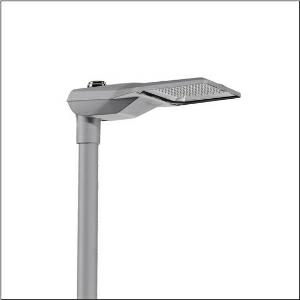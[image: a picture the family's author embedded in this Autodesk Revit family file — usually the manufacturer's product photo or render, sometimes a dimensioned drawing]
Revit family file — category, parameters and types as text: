
# Revit family: streetlight_sl_21_midi___stw1_0a_5xe7e47n08mb_f37a
name_source: partatom
category: Lighting Fixtures
units: mm (PartAtom-declared; Revit-internal decimal feet)

## family parameters
Cut with Voids When Loaded = No
Host = Face
Light Source = No
Part Type = Normal
Room Calculation Point = No
Round Connector Dimension = Use Diameter
Shared = No

## types (1)
- --- (1 x LED, 20180 lm, 147 W, 4000K)
    Apparent Load = 147 VA
    CIE Flux Codes = 38 75 98 100 100
    Color Rendering = 70
    Color Temperature = 4000K
    Default Elevation = 1800 mm
    Description = Streetlight SL 21 midi, mast luminaire, primary light control with lens, of PMMA, primary optical cover: cover, of toughened safety glass, transparent, light distribution: STW1.0a, light emission: direct distribution, primary light characteristic: asymmetric, installation type: side-entry, LED, 3G 2.5mm², High Power LED, rated luminous flux: 20.180lm, luminous efficacy: 137lm/W, light colour: 740, colour temperature: 4000K, control gear: NEMA (7pin), control: overheat protection, pre-setting: linear dimming characteristic, constant luminous flux control, time-dependent luminous flux control, flexible luminous flux parameterisation, mains connection: 220..240V, AC, 50/60Hz, connection cable pre-assembled, cable length: 12,5m, wiring characteristics: H05VV-F, start of lifetime: 147W, end of service life: 155W, reduction: 65W, luminaire housing, of diecast aluminium (EN AC-44300), powder-coated, Siteco® metallic grey (DB 702S), corrosivity category C5 mid according to DIN EN ISO 12944, multi-level sealing system, sealing non-destructively replaceable, inclination adjustable: 0°, 5°, 10°, 15°, length: 644mm, width: 335mm, height: 110mm, spigot size: 42mm (side-entry), mounting height: 4..8m, protection rating (complete): IP66, insulation class (complete): insulation class I (protective earthing), certification: CE, ENEC, ENEC+, VDE, impact resistance: IK10, permissible operating ambient temperature for outdoor applications: -40..+50°C, standard-compliant lighting for roads and squares, packaging unit: 1 piece

Light Distribution: STW1.0a
    Height = 111 mm
    Lamp = 1 x LED
    Lamp Light Flux = 20180 lm
    Lamp Power = 147 W
    Lamp count = 1
    Length = 644 mm
    Luminous efficacy = 137 lm/W
    Manufacturer = Siteco
    ModVariant = No
    Model = 5XE7E47N08MB
    Number of Poles = 1
    OnlyDefault = Yes
    Power Factor = 1
    Product Name = Streetlight SL 21 midi | STW1.0a
    Product group = mast luminaire | pylon top
    ProductGroupID = 6100
    Protection Class = Protection class I
    Protection Degree = IP 66
    RLX_Detail_Level = 1
    RLX_Emergency_Light_Flux = 0 lm
    RLX_Emergency_Type = 0
    RLX_Emergency_Type_DB = No
    RlxData = <blob elided: 26581 chars, md5=7e91a425>
    Socket = socket
    Standby Power = 0 W
    System Light Flux = 20180 lm
    System Power = 147 W
    Type Comments = factory setting: luminous flux: 100 % | dim-lin: 254 | 750 mA
    Type Image = l_1294377.jpg
    URL = http://relux.com
    VarID = @adj_156921
    Voltage = 0 V
    Weight = 0.00 kg
    Width = 336 mm

## geometry (parser evidence)
native form markers: Blend x4, Sweep x11
no freeform markers — native parametric forms only
